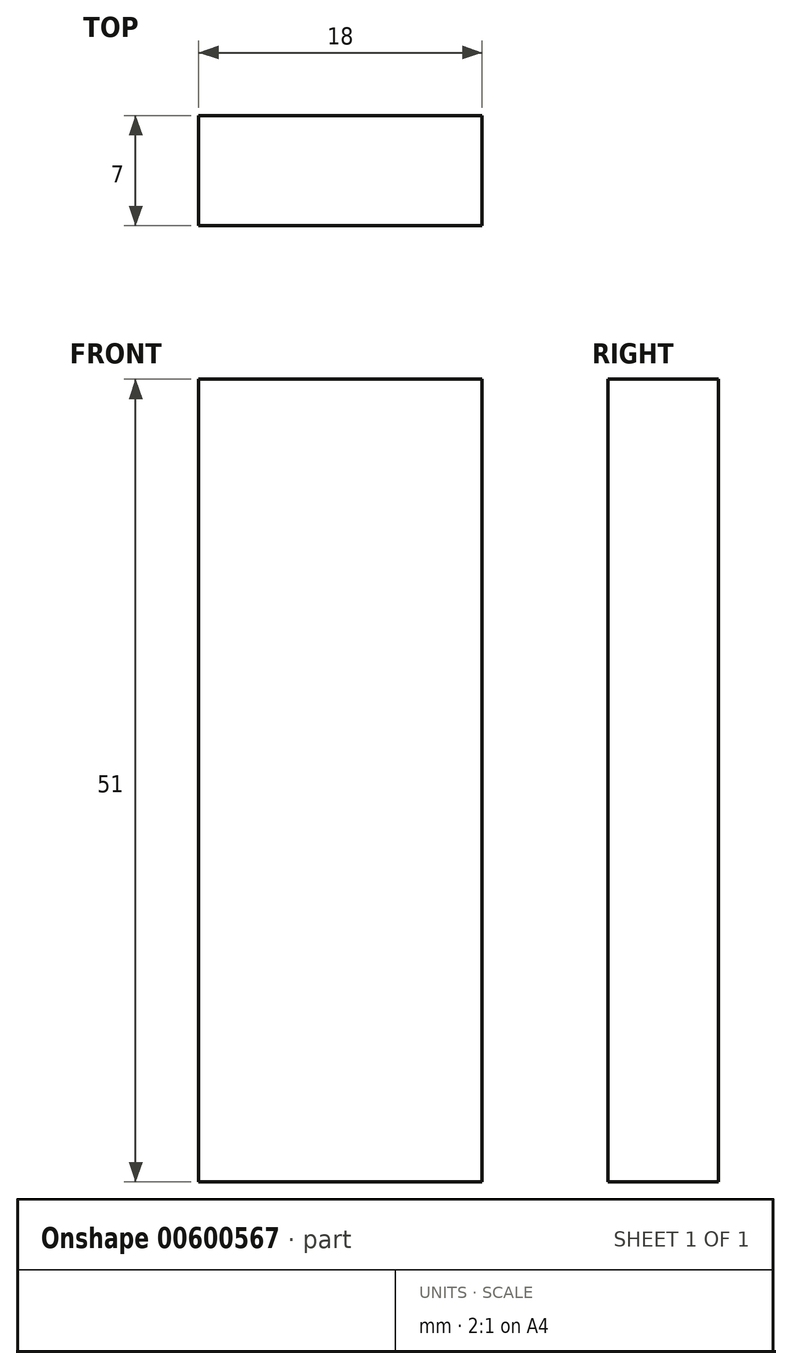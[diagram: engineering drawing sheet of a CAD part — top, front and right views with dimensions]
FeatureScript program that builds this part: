
annotation { "Feature Type Name" : "Feature", "Feature Type Description" : "" }
export const myFeature = defineFeature(function(context is Context, id is Id, definition is map)
    precondition{}
    {
        {
            var Q0;
            Q0=qCreatedBy(makeId("Front.planeOp"),FACE);
            var sketch = newSketch(context, id + "F0", { "sketchPlane" : qUnion([Q0])});
            skLineSegment(sketch, "E0.bottom", {"start": v(9, 25.5) * mm, "end": v(-9, 25.5) * mm});
            skLineSegment(sketch, "E0.top", {"start": v(9, -25.5) * mm, "end": v(-9, -25.5) * mm});
            skLineSegment(sketch, "E0.left", {"start": v(9, 25.5) * mm, "end": v(9, -25.5) * mm});
            skLineSegment(sketch, "E0.right", {"start": v(-9, 25.5) * mm, "end": v(-9, -25.5) * mm});
            skPoint(sketch, "E0.middle", {"position": v(0, 0) * mm});
            skSolve(sketch);
        }
        {
            var Q0;
            Q0 = qSketchRegion(id + "F0", true);
            extrude(context, id + "F1", {"entities" : qUnion([Q0]), "depth" : 7 * mm, "offsetDistance" : 25 * mm});
        }
    });
